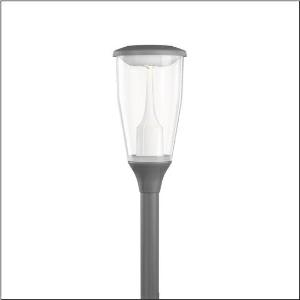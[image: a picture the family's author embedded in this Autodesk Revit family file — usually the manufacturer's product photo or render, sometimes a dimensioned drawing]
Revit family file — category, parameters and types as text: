
# Revit family: dl_11_iq___p1_0a_5xa5575nf14h000022_259a
name_source: partatom
category: Lighting Fixtures
units: mm (PartAtom-declared; Revit-internal decimal feet)

## family parameters
Cut with Voids When Loaded = No
Host = Face
Light Source = No
Part Type = Normal
Room Calculation Point = No
Round Connector Dimension = Use Diameter
Shared = No

## types (1)
- --- (1 x LED, 1530 lm, 11.8 W, 2700K)
    Apparent Load = 12 VA
    CIE Flux Codes = 34 63 91 95 100
    Color Rendering = 70
    Color Temperature = 2700K
    Default Elevation = 1800 mm
    Description = DL 11 iQ, mast luminaire, Module 540 iQ-SR, primary light control with 3 zone facetted reflector, of plastic, silver coated, highly specular, structured, primary optical cover: cover, of PMMA, transparent, light distribution: P1.0a, light emission: direct distribution, primary light characteristic: asymmetric, installation type: post-top, LED, High Power LED, rated luminous flux: 1.560lm, luminous efficacy: 149lm/W, light colour: 727, colour temperature: 2700K, control: Street-Remote, Auto-Match, Temp-Guard, Lumen-Switch, Night-Set, Smart-Wire, Light-Fading, Desk-Remote (wireless, voltage-free reading and setting of iQ features in the workshop via application-optimized NFC function/RFID function), optimised constant luminous flux control (CLO 2.0), mains connection: 220..240V, AC, 50/60Hz, connection cable pre-assembled, cable length: 5,5m, wiring characteristics: H07RN-F, 5-core, 1.5mm², start of lifetime: 12W, end of service life: 12W, reduction: 5W, luminaire housing, upper part, of diecast aluminium, coated, Siteco® metallic grey (DB 702S), spigot size: 76mm (post-top), post-top mast mounting element, of diecast aluminium, coated, Siteco® metallic grey (DB 702S), Module 540 iQ-SR, traffic white (RAL 9016), equipment: standard, protection rating (complete): IP66, insulation class (complete): insulation class II (safety insulation), certification: CE, ENEC, ENEC+, VDE, packaging unit: 1 piece

Light Distribution: P1.0a
    Height = 665 mm
    Lamp = 1 x LED
    Lamp Light Flux = 1530 lm
    Lamp Power = 11.8 W
    Lamp count = 1
    Length = 334 mm
    Luminous efficacy = 130 lm/W
    Manufacturer = Siteco
    ModVariant = No
    Model = 5XA5575NF14H000022
    Number of Poles = 1
    OnlyDefault = Yes
    Power Factor = 1
    Product Name = DL 11 iQ | P1.0a
    Product group = mast luminaire | pylon top
    ProductGroupID = 6100
    Protection Class = Protection class II
    Protection Degree = IP 66
    RLX_Detail_Level = 1
    RLX_Emergency_Light_Flux = 0 lm
    RLX_Emergency_Type = 0
    RLX_Emergency_Type_DB = No
    RlxData = <blob elided: 103469 chars, md5=549c632f>
    Socket = socket
    Standby Power = 0 W
    System Light Flux = 1530 lm
    System Power = 12 W
    Type Comments = factory setting: luminous flux: 100 % | dim-lin: 254 | 472 mA
    Type Image = l_1258354.jpg
    URL = http://relux.com
    VarID = @adj_024085
    Voltage = 0 V
    Weight = 0.00 kg
    Width = 0 mm  [stored 0 ft]

note: [stored X ft] marks values corroborated as IEEE doubles in the binary element streams (Revit-internal decimal feet)

## geometry (parser evidence)
native form markers: Blend x4, Sweep x12
no freeform markers — native parametric forms only
